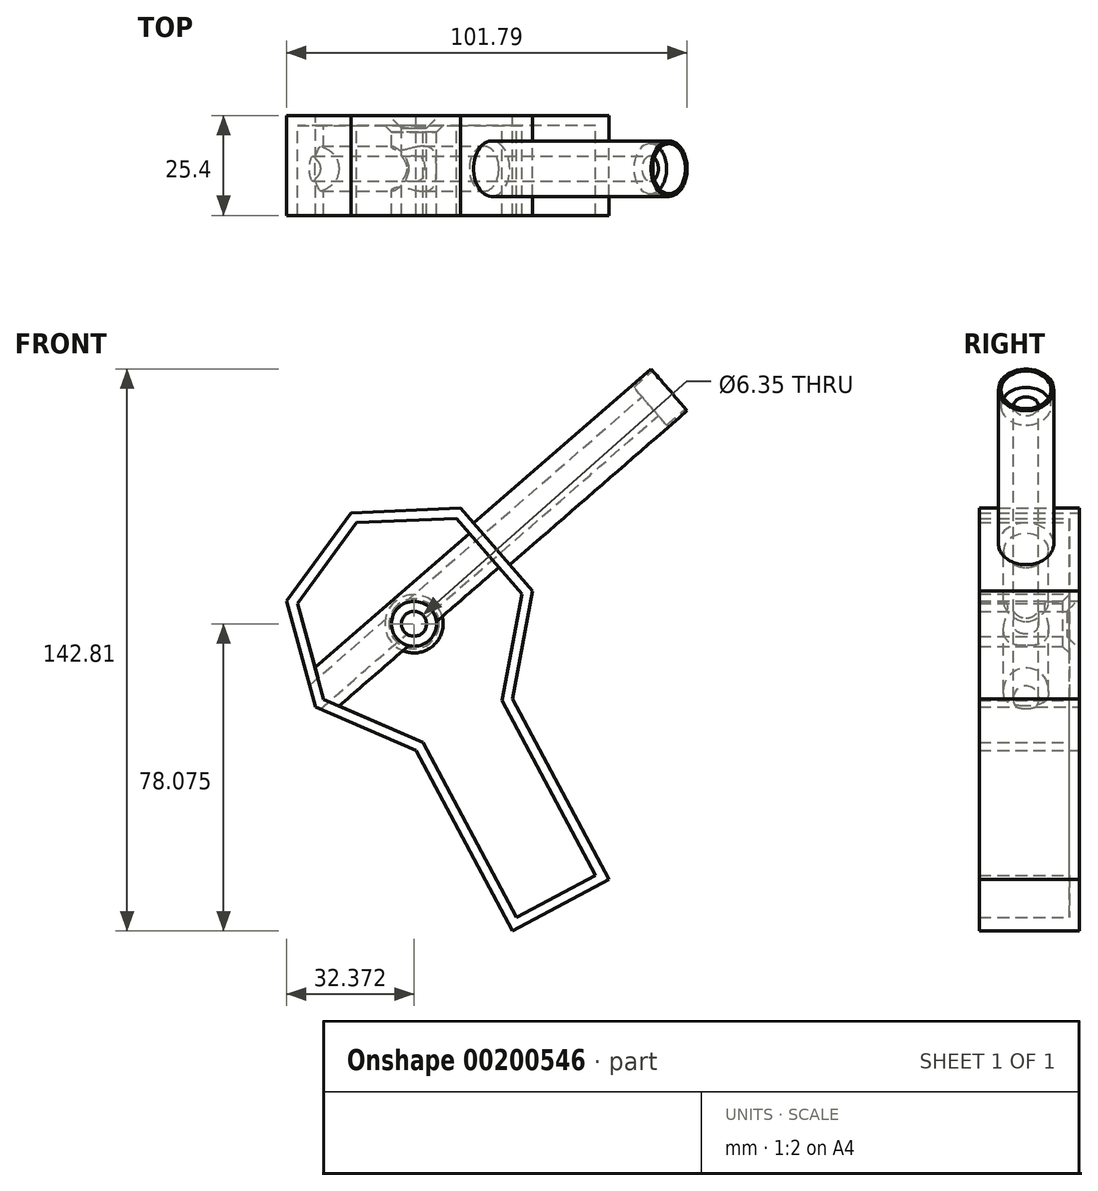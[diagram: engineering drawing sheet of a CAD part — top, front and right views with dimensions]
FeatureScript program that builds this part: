
annotation { "Feature Type Name" : "Feature", "Feature Type Description" : "" }
export const myFeature = defineFeature(function(context is Context, id is Id, definition is map)
    precondition{}
    {
        {
            var Q0;
            Q0=qCreatedBy(makeId("Front.planeOp"),FACE);
            var sketch = newSketch(context, id + "F0", { "sketchPlane" : qUnion([Q0])});
            skCircle(sketch, "E0.cCircle", {"center": v(-40.75, 18.94) * mm, "radius": 32.08 * mm, "construction": true});
            skLineSegment(sketch, "E0.0", {"start": v(-14.86, 0) * mm, "end": v(-39.42, -13.11) * mm});
            skLineSegment(sketch, "E0.1", {"start": v(-39.42, -13.11) * mm, "end": v(-64.98, -2.09) * mm});
            skLineSegment(sketch, "E0.2", {"start": v(-64.98, -2.09) * mm, "end": v(-72.3, 24.77) * mm});
            skLineSegment(sketch, "E0.3", {"start": v(-72.3, 24.77) * mm, "end": v(-55.86, 47.23) * mm});
            skLineSegment(sketch, "E0.4", {"start": v(-55.86, 47.23) * mm, "end": v(-28.05, 48.4) * mm});
            skLineSegment(sketch, "E0.5", {"start": v(-28.05, 48.4) * mm, "end": v(-9.8, 27.37) * mm});
            skLineSegment(sketch, "E0.6", {"start": v(-9.8, 27.37) * mm, "end": v(-14.86, 0) * mm});
            skSolve(sketch);
        }
        {
            var Q0;
            Q0 = qSketchRegion(id + "F0", true);
            extrude(context, id + "F1", {"entities" : qUnion([Q0]), "depth" : 25.4 * mm});
        }
        {
            var Q0;
            Q0=makeQuery(id+"F1.opExtrude","SWEPT_FACE",FACE,{"disambiguationData":[OSD([sQuery(id+"F0.wireOp",EDGE,"E0.0")])]});
            extrude(context, id + "F2", {"entities" : qUnion([Q0]), "operationType" : NewBodyOperationType.ADD, "depth" : 52.07 * mm});
        }
        {
            var Q0;
            Q0=qCreatedBy(makeId("Front.planeOp"),FACE);
            var sketch = newSketch(context, id + "F3", { "sketchPlane" : qUnion([Q0])});
            skCircle(sketch, "E1", {"center": v(-39.93, 19.04) * mm, "radius": 13.57 * mm});
            skSolve(sketch);
        }
        {
            var Q0;
            Q0=sQuery(id+"F3.wireOp",VERTEX,"E1.center");
            var Q1;
            Q1=makeQuery(id+"F1.opExtrude","SWEPT_BODY",BODY,{"disambiguationData":[OSD([sQuery(id+"F0.wireOp",EDGE,"E0.0"),sQuery(id+"F0.wireOp",EDGE,"E0.1"),sQuery(id+"F0.wireOp",EDGE,"E0.2"),sQuery(id+"F0.wireOp",EDGE,"E0.3"),sQuery(id+"F0.wireOp",EDGE,"E0.4"),sQuery(id+"F0.wireOp",EDGE,"E0.5"),sQuery(id+"F0.wireOp",EDGE,"E0.6")])]});
            hole(context, id + "F4", {"style" : HoleStyle.C_SINK, "endStyle" : HoleEndStyle.THROUGH, "oppositeDirection" : true, "holeDiameter" : 6.35 * mm, "cSinkDiameter" : 12.7 * mm, "cSinkAngle" : 90 * degree, "startFromSketch" : true, "locations" : qUnion([Q0]), "scope" : qUnion([Q1]), "isTappedThrough" : true});
        }
        {
            var Q0;
            Q0=makeQuery(id+"F1.opExtrude","SWEPT_FACE",FACE,{"disambiguationData":[OSD([sQuery(id+"F0.wireOp",EDGE,"E0.5")])]});
            var sketch = newSketch(context, id + "F5", { "sketchPlane" : qUnion([Q0])});
            skCircle(sketch, "E2", {"center": v(-13.51, 42.95) * mm, "radius": 7.02 * mm});
            skSolve(sketch);
        }
        {
            var Q0;
            Q0 = qSketchRegion(id + "F5", true);
            extrude(context, id + "F6", {"entities" : qUnion([Q0]), "operationType" : NewBodyOperationType.ADD, "depth" : 59.69 * mm});
        }
        {
            var Q0;
            Q0=makeQuery(id+"F6.opExtrude","CAP_FACE",FACE,{"disambiguationData":[OSD([sQuery(id+"F5.wireOp",EDGE,"E2")])],"isStart":false});
            var sketch = newSketch(context, id + "F7", { "sketchPlane" : qUnion([Q0])});
            skCircle(sketch, "E3", {"center": v(-13.51, 42.95) * mm, "radius": 4.7 * mm});
            skSolve(sketch);
        }
        {
            var Q0;
            Q0=sQuery(id+"F7.wireOp",VERTEX,"E3.center");
            var Q1;
            Q1=makeQuery(id+"F1.opExtrude","SWEPT_BODY",BODY,{"disambiguationData":[OSD([sQuery(id+"F0.wireOp",EDGE,"E0.0"),sQuery(id+"F0.wireOp",EDGE,"E0.1"),sQuery(id+"F0.wireOp",EDGE,"E0.2"),sQuery(id+"F0.wireOp",EDGE,"E0.3"),sQuery(id+"F0.wireOp",EDGE,"E0.4"),sQuery(id+"F0.wireOp",EDGE,"E0.5"),sQuery(id+"F0.wireOp",EDGE,"E0.6")])]});
            hole(context, id + "F8", {"style" : HoleStyle.C_BORE, "endStyle" : HoleEndStyle.THROUGH, "holeDiameter" : 6.35 * mm, "cBoreDiameter" : 12.7 * mm, "cBoreDepth" : 6.35 * mm, "startFromSketch" : true, "locations" : qUnion([Q0]), "scope" : qUnion([Q1]), "isTappedThrough" : true});
        }
        {
            var Q0;
            {var subQ0=sQuery(id+"F0.wireOp",EDGE,"E0.0");Q0=makeQuery(id+"F2.boolean.opBoolean","MERGE",FACE,{"derivedFrom":[makeQuery(id+"F1.opExtrude","CAP_FACE",FACE,{"disambiguationData":[OSD([subQ0,sQuery(id+"F0.wireOp",EDGE,"E0.1"),sQuery(id+"F0.wireOp",EDGE,"E0.2"),sQuery(id+"F0.wireOp",EDGE,"E0.3"),sQuery(id+"F0.wireOp",EDGE,"E0.4"),sQuery(id+"F0.wireOp",EDGE,"E0.5"),sQuery(id+"F0.wireOp",EDGE,"E0.6")])],"isStart":false}),makeQuery(id+"F2.opExtrude","SWEPT_FACE",FACE,{"disambiguationData":[OSD([subQ0]),TDD([makeQuery(id+"F1.opExtrude","CAP_EDGE",EDGE,{"disambiguationData":[OSD([subQ0])],"isStart":false})])]})]});}
            shell(context, id + "F9", {"entities" : qUnion([Q0]), "thickness" : 2.54 * mm});
        }
    });
